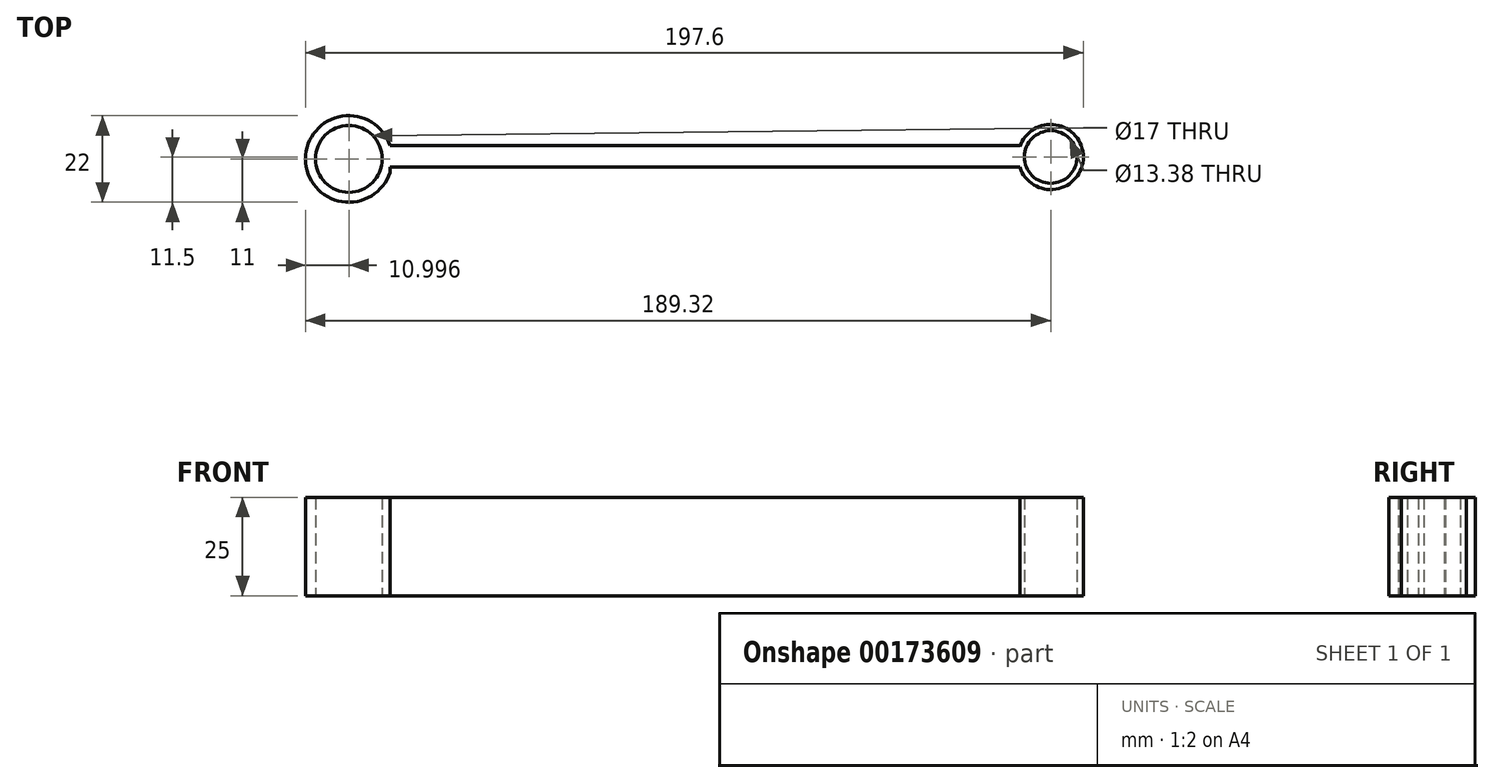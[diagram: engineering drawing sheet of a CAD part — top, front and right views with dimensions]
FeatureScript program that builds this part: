
annotation { "Feature Type Name" : "Feature", "Feature Type Description" : "" }
export const myFeature = defineFeature(function(context is Context, id is Id, definition is map)
    precondition{}
    {
        {
            var Q0;
            Q0=qCreatedBy(makeId("Top.planeOp"),FACE);
            var sketch = newSketch(context, id + "F0", { "sketchPlane" : qUnion([Q0])});
            skArc(sketch, "E0", {"start": v(-12.1, 41.02) * mm, "mid": v(-33.56, 37.63) * mm, "end": v(-12.1, 34.23) * mm});
            skCircle(sketch, "E1", {"center": v(-22.56, 37.63) * mm, "radius": 8.5 * mm});
            skArc(sketch, "E2", {"start": v(147.9, 35.52) * mm, "mid": v(164.04, 38.13) * mm, "end": v(147.9, 40.74) * mm});
            skCircle(sketch, "E3", {"center": v(155.76, 38.13) * mm, "radius": 6.7 * mm});
            skLineSegment(sketch, "E4.bottom", {"start": v(-12.1, 41.02) * mm, "end": v(147.9, 41.02) * mm});
            skLineSegment(sketch, "E4.top", {"start": v(-12.1, 35.52) * mm, "end": v(147.9, 35.52) * mm});
            skLineSegment(sketch, "E4.left", {"start": v(-12.1, 35.52) * mm, "end": v(-12.1, 34.23) * mm});
            skLineSegment(sketch, "E4.right", {"start": v(147.9, 41.02) * mm, "end": v(147.9, 40.74) * mm});
            skSolve(sketch);
        }
        {
            var Q0;
            {var subQ4=sQuery(id+"F0.wireOp",EDGE,"E0");Q0=makeQuery(id+"F0.imprint","IMPRINT",FACE,{"disambiguationData":[TD([[makeQuery(id+"F0.imprint","IMPRINT",EDGE,{"derivedFrom":subQ4}),1.0]])]});}
            var Q1;
            {var subQ1=sQuery(id+"F0.wireOp",EDGE,"E2");Q1=makeQuery(id+"F0.imprint","IMPRINT",FACE,{"disambiguationData":[TD([[makeQuery(id+"F0.imprint","IMPRINT",EDGE,{"derivedFrom":subQ1}),1.0]])]});}
            var Q2;
            Q2=makeQuery(id+"F0.imprint","IMPRINT",FACE,{"disambiguationData":[TD([[makeQuery(id+"F0.imprint","IMPRINT",EDGE,{"derivedFrom":sQuery(id+"F0.wireOp",EDGE,"ppHGRZ6R-xUdv-7O5b-t3ip-gmee00dXwYxm.bottom")}),-1.0]])]});
            extrude(context, id + "F1", {"entities" : qUnion([Q0, Q1, Q2]), "depth" : 25 * mm});
        }
    });
